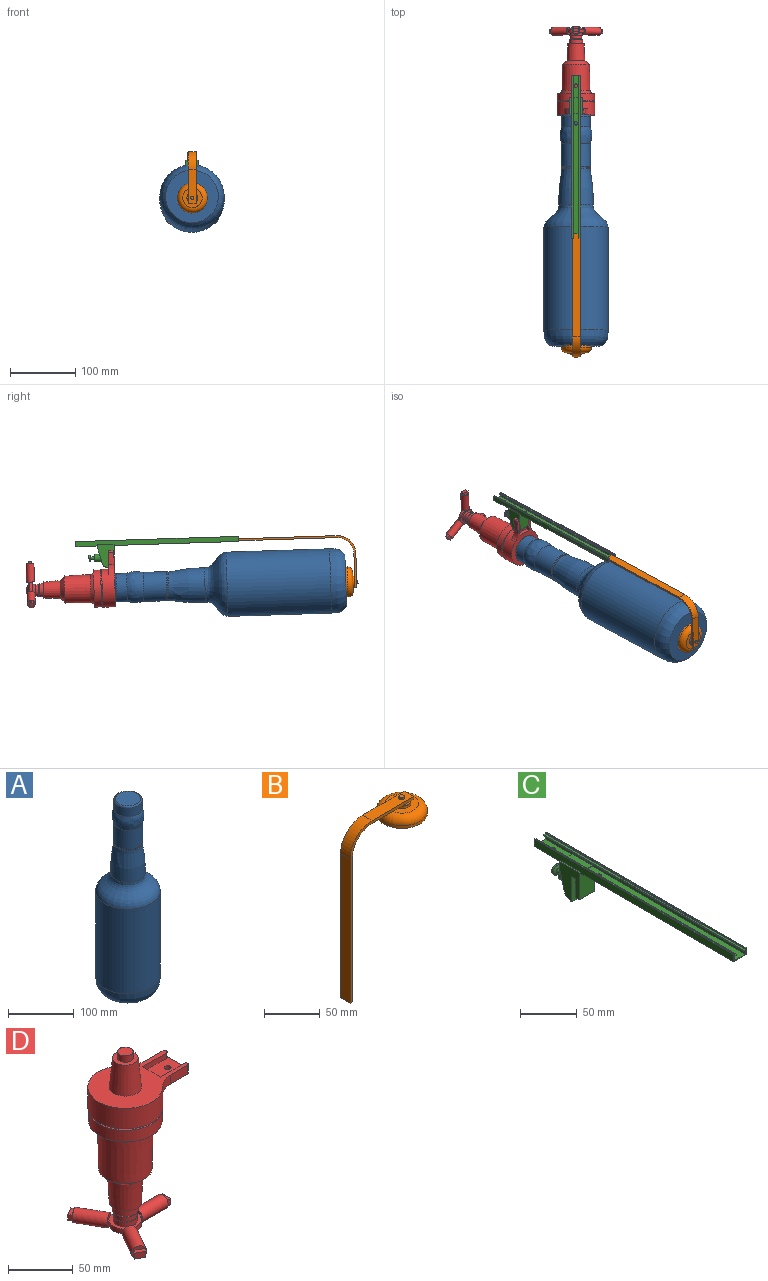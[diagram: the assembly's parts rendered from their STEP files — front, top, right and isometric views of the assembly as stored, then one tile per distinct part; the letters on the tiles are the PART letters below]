
ASSEMBLY  parts=4 mates=8
PART A: 20 faces, bbox 98.6x98.6x353.6 mm
  f0: revolved ~55.93x53.24mm, area 8868.7mm2, adj f1,f5
  f1: revolved ~44.25x44.25mm, area 232mm2, adj f0,f6
  f2: plane 80.75x80.75mm, normal (0,0,-1), area 5121.6mm2, adj f3
  f3: revolved ~98.59x98.59mm, area 7591.1mm2, adj f2,f4
  f4: cylinder r=49.27mm len=158.7mm, axis (0,0,-1), area 49125.5mm2, adj f3,f5
  f5: revolved ~98.53x98.53mm, area 9997.1mm2, adj f0,f4
  f6: revolved ~44.72x44.72mm, area 170.7mm2, adj f1,f7
  f7: cylinder r=22.36mm len=44.72mm, axis (0,0,-1), area 4981mm2, adj f6,f8
  f8: bspline ~48.27x47.63mm, area 3805.5mm2, adj f7,f9
  f9: cylinder r=21.7mm len=43.4mm, axis (0,0,-1), area 2170.4mm2, adj f8,f11
  f10: plane 38.32x38.32mm, normal (0,0,1), area 1153.4mm2, adj f11
  f11: torus R=19.16mm, axis (0,0,1), area 520.9mm2, adj f9,f10
  f12: revolved ~55.91x43.08mm, area 7056.8mm2, adj f17,f18
  f13: plane 34.56x34.56mm, normal (0,0,-1), area 938.1mm2, adj f19
  f14: plane 77.1x77.1mm, normal (0,0,1), area 4668.7mm2, adj f15
  f15: revolved ~88.43x88.43mm, area 5230mm2, adj f14,f16
  f16: cylinder r=44.19mm len=158.42mm, axis (0,0,-1), area 43983mm2, adj f15,f17
  f17: revolved ~88.37x88.37mm, area 8539mm2, adj f12,f16
  f18: revolved ~34.56x34.56mm, area 522.8mm2, adj f12,f19
  f19: cylinder r=17.28mm len=34.56mm, axis (0,0,-1), area 3082.6mm2, adj f13,f18
PART B: 23 faces, bbox 96.4x49.8x187.8 mm
  f0: plane 12x3.84mm, normal (0,0,-1), area 24.6mm2, adj f6,f9,f10,f18
  f1: plane 37.84x12mm, normal (0,0,-1), area 432.6mm2, adj f5,f9,f10,f18
  f2: plane 53x12mm, normal (0,0,1), area 616.4mm2, adj f6,f7,f9,f10,f21
  f3: plane 12x3mm, normal (0,0,-1), area 36mm2, adj f4,f8,f9,f10
  f4: plane 158x12mm, normal (1,0,0), area 1896mm2, adj f3,f5,f9,f10
  f5: cylinder r=25mm len=25mm, axis (0,1,0), area 471.2mm2, adj f1,f4,f9,f10
  f6: plane 12x3mm, normal (1,0,0), area 36mm2, adj f0,f2,f9,f10
  f7: cylinder r=28mm len=28mm, axis (0,1,0), area 527.8mm2, adj f2,f8,f9,f10
  f8: plane 158x12mm, normal (-1,0,0), area 1896mm2, adj f3,f7,f9,f10
  f9: plane 186x81mm, normal (0,-1,0), area 757.9mm2, adj f0,f1,f2,f3,f4,f5,f6,f7
  f10: plane 186x81mm, normal (0,1,0), area 757.9mm2, adj f0,f1,f2,f3,f4,f5,f6,f7
  f11: plane 30x30mm, normal (0,0,-1), area 706.9mm2, adj f12
  f12: torus R=15mm, axis (0,0,-1), area 1114.5mm2, adj f11,f13
  f13: cylinder r=21mm len=42mm, axis (0,0,-1), area 395.8mm2, adj f12,f14
  f14: plane 46x46mm, normal (0,0,-1), area 276.5mm2, adj f13,f15
  f15: cylinder r=23mm len=46mm, axis (0,0,-1), area 433.5mm2, adj f14,f16
  f16: torus R=15mm, axis (0,0,-1), area 1586.5mm2, adj f15,f17
  f17: plane 30x30mm, normal (0,0,1), area 493mm2, adj f16,f18
  f18: cylinder r=8.25mm len=16.5mm, axis (0,0,-1), area 155.5mm2, adj f0,f1,f17,f19,f20
  f19: plane 11.32x2.25mm, normal (0,0,1), area 17.5mm2, adj f10,f18
  f20: plane 11.32x2.25mm, normal (0,0,1), area 17.5mm2, adj f9,f18
  f21: cylinder r=2.5mm len=5mm, axis (0,0,-1), area 28.3mm2, adj f2,f22
  f22: plane 5x5mm, normal (0,0,1), area 19.6mm2, adj f21
PART C: 50 faces, bbox 19.2x249x42 mm
  f0: cylinder r=10mm len=19.2mm, axis (-1,0,0), area 94.7mm2, adj f1,f34,f36,f37,f38,f39,f40
  f1: plane 22.28x19.2mm, normal (0,0.97,-0.26), area 175mm2, adj f0,f35,f36,f37,f39,f40,f41
  f2: plane 249x7.7mm, normal (-1,0,0), area 1879.8mm2, adj f3,f4,f12,f20,f21,f27,f29,f30
  f3: plane 190.5x15mm, normal (0,0,-1), area 2833.7mm2, adj f2,f5,f20,f23,f29
  f4: plane 33.5x15mm, normal (0,0,-1), area 478.7mm2, adj f2,f5,f21,f22,f30
  f5: plane 249x7.7mm, normal (1,0,0), area 1879.8mm2, adj f3,f4,f13,f20,f21,f28,f29,f30
  f6: plane 249x4.5mm, normal (-1,0,0), area 1108mm2, adj f7,f8,f17,f20,f21,f24,f25,f26
  f7: plane 190.5x13mm, normal (0,0,1), area 2452.7mm2, adj f6,f9,f20,f23,f25
  f8: plane 33.5x13mm, normal (0,0,1), area 411.7mm2, adj f6,f9,f21,f22,f24
  f9: plane 249x4.5mm, normal (1,0,0), area 1108mm2, adj f7,f8,f18,f20,f21,f24,f25,f26
  f10: plane 249x2mm, normal (0,0,1), area 498mm2, adj f11,f19,f20,f21
  f11: plane 249x1.2mm, normal (1,0,0), area 298.8mm2, adj f10,f12,f20,f21
  f12: plane 249x1mm, normal (0,0,1), area 249mm2, adj f2,f11,f20,f21
  f13: plane 249x1mm, normal (0,0,1), area 249mm2, adj f5,f14,f20,f21
  f14: plane 249x1.2mm, normal (-1,0,0), area 298.8mm2, adj f13,f15,f20,f21
  f15: plane 249x2mm, normal (0,0,1), area 498mm2, adj f14,f16,f20,f21
  f16: plane 249x1mm, normal (-1,0,0), area 249mm2, adj f15,f17,f20,f21
  f17: plane 249x2mm, normal (0,0,-1), area 498mm2, adj f6,f16,f20,f21
  f18: plane 249x2mm, normal (0,0,-1), area 498mm2, adj f9,f19,f20,f21
  f19: plane 249x1mm, normal (1,0,0), area 249mm2, adj f10,f18,f20,f21
  f20: plane 15x7.7mm, normal (0,-1,0), area 32.4mm2, adj f2,f3,f5,f6,f7,f9,f10,f11
  f21: plane 15x7.7mm, normal (0,1,0), area 32.4mm2, adj f2,f4,f5,f6,f8,f9,f10,f11
  f22: cylinder r=2.75mm len=5.5mm, axis (0,0,-1), area 17.3mm2, adj f4,f8
  f23: cylinder r=2.75mm len=5.5mm, axis (0,0,-1), area 17.3mm2, adj f3,f7
  f24: plane 13x0.5mm, normal (0,1,0), area 6.5mm2, adj f6,f8,f9,f26
  f25: plane 13x0.5mm, normal (0,-1,0), area 6.5mm2, adj f6,f7,f9,f26
  f26: plane 25x13mm, normal (0,0,1), area 325mm2, adj f6,f9,f24,f25
  f27: plane 25x2.1mm, normal (0,0,1), area 52.5mm2, adj f2,f29,f30,f37
  f28: plane 25x2.1mm, normal (0,0,1), area 52.5mm2, adj f5,f29,f30,f36
  f29: plane 29x19.2mm, normal (0,-1,0), area 534.3mm2, adj f2,f3,f5,f27,f28,f31,f36,f37
  f30: plane 19.2x4.81mm, normal (0,1,0), area 69.9mm2, adj f2,f4,f5,f27,f28,f35,f36,f37
  f31: plane 19.2x5mm, normal (0,0,-1), area 96mm2, adj f29,f32,f36,f37
  f32: plane 20.2x19.2mm, normal (0,1,0), area 387.8mm2, adj f31,f33,f36,f37
  f33: plane 19.2x4.2mm, normal (0,0,-1), area 80.6mm2, adj f32,f34,f36,f37
  f34: plane 27x19.2mm, normal (0,-1,0), area 504.5mm2, adj f0,f33,f36,f37,f49
  f35: cylinder r=5mm len=19.2mm, axis (-1,0,0), area 25.1mm2, adj f1,f30,f36,f37
  f36: plane 35.8x25mm, normal (1,0,0), area 613.1mm2, adj f0,f1,f28,f29,f30,f31,f32,f33
  f37: plane 35.8x25mm, normal (-1,0,0), area 613.1mm2, adj f0,f1,f27,f29,f30,f31,f32,f33
  f38: plane 23.54x15.6mm, normal (0,1,0), area 261.5mm2, adj f0,f39,f40,f41,f47
  f39: plane 23.54x11.1mm, normal (1,0,0), area 178.5mm2, adj f0,f1,f38,f41
  f40: plane 23.54x11.1mm, normal (-1,0,0), area 178.5mm2, adj f0,f1,f38,f41
  f41: plane 15.6x11.1mm, normal (0,0,-1), area 173.2mm2, adj f1,f38,f39,f40
  f42: plane 10x10mm, normal (0,1,0), area 78.5mm2, adj f43
  f43: cylinder r=5mm len=10mm, axis (0,1,0), area 62.8mm2, adj f42,f44
  f44: cone r=5mm half-angle=69.7deg, axis (0,1,0), area 66mm2, adj f43,f45
  f45: cylinder r=2.3mm len=6mm, axis (0,1,0), area 86.7mm2, adj f44,f46
  f46: plane 11.6x11.6mm, normal (0,1,0), area 89.1mm2, adj f45,f47
  f47: cylinder r=5.8mm len=17.8mm, axis (0,1,0), area 648.7mm2, adj f38,f46
  f48: plane 4.2x4.2mm, normal (0,-1,0), area 13.9mm2, adj f49
  f49: cylinder r=2.1mm len=4.2mm, axis (0,1,0), area 33mm2, adj f34,f48
PART D: 79 faces, bbox 85.6x82.5x169.8 mm
  f0: plane 27.02x25.5mm, normal (0,0,1), area 237.2mm2, adj f1,f2,f4,f5,f7,f8,f12,f13
  f1: plane 5.56x2.83mm, normal (-0.87,0.5,0), area 8.3mm2, adj f0,f3,f11,f13,f53
  f2: plane 5.56x2.83mm, normal (0.87,-0.5,0), area 8.3mm2, adj f0,f3,f11,f12,f53
  f3: plane 9.4x7.28mm, normal (0,0,-1), area 22.9mm2, adj f1,f2,f11,f53
  f4: plane 5.56x2.83mm, normal (0.87,0.5,0), area 8.3mm2, adj f0,f6,f11,f14,f45
  f5: plane 5.56x2.83mm, normal (-0.87,-0.5,0), area 8.3mm2, adj f0,f6,f11,f13,f45
  f6: plane 9.4x7.28mm, normal (0,0,-1), area 22.9mm2, adj f4,f5,f11,f45
  f7: plane 5.56x3.26mm, normal (0,1,0), area 8.3mm2, adj f0,f9,f11,f14,f37
  f8: plane 5.56x3.26mm, normal (0,-1,0), area 8.3mm2, adj f0,f9,f11,f12,f37
  f9: plane 9x3.21mm, normal (0,0,-1), area 22.9mm2, adj f7,f8,f11,f37
  f10: cylinder r=4mm len=8mm, axis (0,0,1), area 113.1mm2, adj f15,f35
  f11: cone r=12.5mm half-angle=59.9deg, axis (0,0,1), area 430.2mm2, adj f1,f2,f3,f4,f5,f6,f7,f8
  f12: cylinder r=12.5mm len=13.6mm, axis (0,0,1), area 76.4mm2, adj f0,f2,f8,f11
  f13: cylinder r=12.5mm len=15.7mm, axis (0,0,1), area 76.4mm2, adj f0,f1,f5,f11
  f14: cylinder r=12.5mm len=13.6mm, axis (0,0,1), area 76.4mm2, adj f0,f4,f7,f11
  f15: plane 9.5x9.5mm, normal (0,0,-1), area 20.6mm2, adj f10,f16
  f16: cylinder r=4.75mm len=9.5mm, axis (0,0,1), area 29.8mm2, adj f11,f15
  f17: cylinder r=9.35mm len=18.7mm, axis (0,0,1), area 264.4mm2, adj f0,f18
  f18: plane 18.7x18.7mm, normal (0,0,1), area 20.2mm2, adj f17,f19
  f19: cylinder r=9mm len=18mm, axis (0,0,1), area 254.5mm2, adj f18,f20
  f20: plane 18x18mm, normal (0,0,1), area 141.4mm2, adj f19,f21
  f21: cylinder r=6mm len=12mm, axis (0,0,1), area 56.5mm2, adj f20,f22
  f22: plane 20.6x20.6mm, normal (0,0,-1), area 220.2mm2, adj f21,f23
  f23: cylinder r=10.3mm len=20.6mm, axis (0,0,1), area 420.7mm2, adj f22,f24
  f24: plane 25x25mm, normal (0,0,-1), area 157.6mm2, adj f23,f25
  f25: cone r=13.75mm half-angle=2.8deg, axis (0,0,1), area 2146.6mm2, adj f24,f26
  f26: cone r=20.75mm half-angle=49.4deg, axis (0,0,1), area 999.3mm2, adj f25,f27
  f27: cone r=21.5mm half-angle=1.1deg, axis (0,0,1), area 5310.2mm2, adj f26,f28
  f28: cone r=24mm half-angle=26.6deg, axis (0,0,1), area 799.1mm2, adj f27,f29
  f29: plane 57x57mm, normal (0,0,-1), area 742.2mm2, adj f28,f30
  f30: cylinder r=28.5mm len=57mm, axis (0,0,1), area 1969.8mm2, adj f29,f31
  f31: plane 57x57mm, normal (0,0,1), area 508.9mm2, adj f30,f32
  f32: cylinder r=25.5mm len=51mm, axis (0,0,1), area 272.4mm2, adj f31,f33
  f33: plane 58x58mm, normal (0,0,-1), area 599.3mm2, adj f32,f34
  f34: cylinder r=29mm len=58mm, axis (0,0,1), area 3182mm2, adj f33,f60,f61,f67,f68
  f35: plane 8x8mm, normal (0,0,-1), area 50.3mm2, adj f10
  f36: cylinder r=6mm len=28mm, axis (1,0,0), area 1055.6mm2, adj f37,f38
  f37: plane 12x12mm, normal (-1,0,0), area 63.6mm2, adj f0,f7,f8,f9,f36
  f38: plane 12x12mm, normal (1,0,0), area 63.6mm2, adj f36,f40,f41,f42,f43
  f39: plane 9x5.5mm, normal (1,0,0), area 49.5mm2, adj f40,f41,f42,f43
  f40: plane 9x4mm, normal (0,0,-1), area 36mm2, adj f38,f39,f41,f42
  f41: plane 5.5x4mm, normal (0,-1,0), area 22mm2, adj f38,f39,f40,f43
  f42: plane 5.5x4mm, normal (0,1,0), area 22mm2, adj f38,f39,f40,f43
  f43: plane 9x4mm, normal (0,0,1), area 36mm2, adj f38,f39,f41,f42
  f44: cylinder r=6mm len=30.25mm, axis (-0.5,0.87,0), area 1055.6mm2, adj f45,f46
  f45: plane 12x10.39mm, normal (0.5,-0.87,0), area 63.6mm2, adj f0,f4,f5,f6,f44
  f46: plane 12x10.39mm, normal (-0.5,0.87,0), area 63.6mm2, adj f44,f48,f49,f50,f51
  f47: plane 7.79x5.5mm, normal (-0.5,0.87,0), area 49.5mm2, adj f48,f49,f50,f51
  f48: plane 9.79x7.96mm, normal (0,0,-1), area 36mm2, adj f46,f47,f49,f50
  f49: plane 5.5x3.46mm, normal (-0.87,-0.5,0), area 22mm2, adj f46,f47,f48,f51
  f50: plane 5.5x3.46mm, normal (0.87,0.5,0), area 22mm2, adj f46,f47,f48,f51
  f51: plane 9.79x7.96mm, normal (0,0,1), area 36mm2, adj f46,f47,f49,f50
  f52: cylinder r=6mm len=30.25mm, axis (-0.5,-0.87,0), area 1055.6mm2, adj f53,f54
  f53: plane 12x10.39mm, normal (0.5,0.87,0), area 63.6mm2, adj f0,f1,f2,f3,f52
  f54: plane 12x10.39mm, normal (-0.5,-0.87,0), area 63.6mm2, adj f52,f56,f57,f58,f59
  f55: plane 7.79x5.5mm, normal (-0.5,-0.87,0), area 49.5mm2, adj f56,f57,f58,f59
  f56: plane 9.79x7.96mm, normal (0,0,-1), area 36mm2, adj f54,f55,f57,f58
  f57: plane 5.5x3.46mm, normal (0.87,-0.5,0), area 22mm2, adj f54,f55,f56,f59
  f58: plane 5.5x3.46mm, normal (-0.87,0.5,0), area 22mm2, adj f54,f55,f56,f59
  f59: plane 9.79x7.96mm, normal (0,0,1), area 36mm2, adj f54,f55,f57,f58
  f60: cylinder r=20mm len=14.6mm, axis (0,0,-1), area 139.1mm2, adj f34,f66,f67,f68
  f61: cylinder r=20mm len=14.6mm, axis (0,0,-1), area 139.1mm2, adj f34,f62,f67,f68
  f62: plane 18.99x8.5mm, normal (0,-1,0), area 161.4mm2, adj f61,f63,f67,f68
  f63: cylinder r=1.75mm len=8.5mm, axis (0,0,-1), area 37.1mm2, adj f62,f64,f67,f68,f75,f77
  f64: plane 23.5x3.5mm, normal (1,0,0), area 82.3mm2, adj f63,f65,f68,f77
  f65: cylinder r=1.75mm len=8.5mm, axis (0,0,-1), area 23.4mm2, adj f64,f66,f67,f68,f74
  f66: plane 18.99x8.5mm, normal (0,1,0), area 161.4mm2, adj f60,f65,f67,f68
  f67: plane 85.5x58mm, normal (0,0,1), area 2403.3mm2, adj f34,f60,f61,f62,f63,f65,f66,f72
  f68: plane 39.65x35.34mm, normal (0,0,-1), area 776.7mm2, adj f34,f60,f61,f62,f63,f64,f65,f66
  f69: plane 12x12mm, normal (0,0,1), area 113.1mm2, adj f70
  f70: cylinder r=6mm len=12mm, axis (0,0,1), area 226.2mm2, adj f69,f71
  f71: plane 20x20mm, normal (0,0,1), area 201.1mm2, adj f70,f72
  f72: cone r=10mm half-angle=5.1deg, axis (0,0,-1), area 1947.7mm2, adj f67,f71
  f73: plane 25.75x5mm, normal (0,-1,0), area 128.7mm2, adj f67,f74,f76,f77
  f74: cylinder r=2.25mm len=5mm, axis (0,0,1), area 17.7mm2, adj f65,f67,f73,f77
  f75: plane 26.25x5mm, normal (0,1,0), area 131.2mm2, adj f63,f67,f76,f77
  f76: plane 19.5x5mm, normal (1,0,0), area 97.5mm2, adj f67,f73,f75,f77
  f77: plane 28x23.5mm, normal (0,0,1), area 528.1mm2, adj f63,f64,f73,f74,f75,f76,f78
  f78: cylinder r=2.5mm len=5mm, axis (0,0,1), area 55mm2, adj f68,f77
PLACE A rot(axis=(-0.91,-0.29,-0.28),97deg) t=(114.61,-294.19,-140.79)mm
PLACE B rot(axis=(0.57,0.57,-0.59),118.9deg) t=(115.11,-125.59,-77.18)mm
PLACE C rot(axis=(-1,0,0),1.8deg) t=(114.61,116.52,-88.98)mm
PLACE D rot(axis=(0.57,-0.57,0.59),118.9deg) t=(114.61,192.78,-156.47)mm
MATE parallel D.f75 <-> C.f0  axis (-1,0,0) through (124.61,60.49,-110.56)mm
MATE cylindrical D.f28 <-> A.f4  axis (0,1,-0.03) through (114.61,56.65,-152.09)mm
MATE planar B.f4 <-> C.f7  axis (0,-0.03,-1) through (115.11,-204.65,-77.64)mm
MATE planar D.f68 <-> C.f34  axis (0,1,-0.03) through (114.61,66.49,-110.83)mm
MATE planar B.f12 <-> A.f4  axis (0,1,-0.03) through (115.11,-296.81,-143.2)mm
MATE planar A.f4 <-> D.f28  axis (0,1,-0.03) through (114.61,56.65,-152.09)mm
MATE cylindrical D.f78 <-> C.f43  axis (0,-1,0.03) through (114.61,63.15,-105.77)mm
MATE planar B.f10 <-> C.f6  axis (1,0,0) through (121.11,-242.92,-87.61)mm
